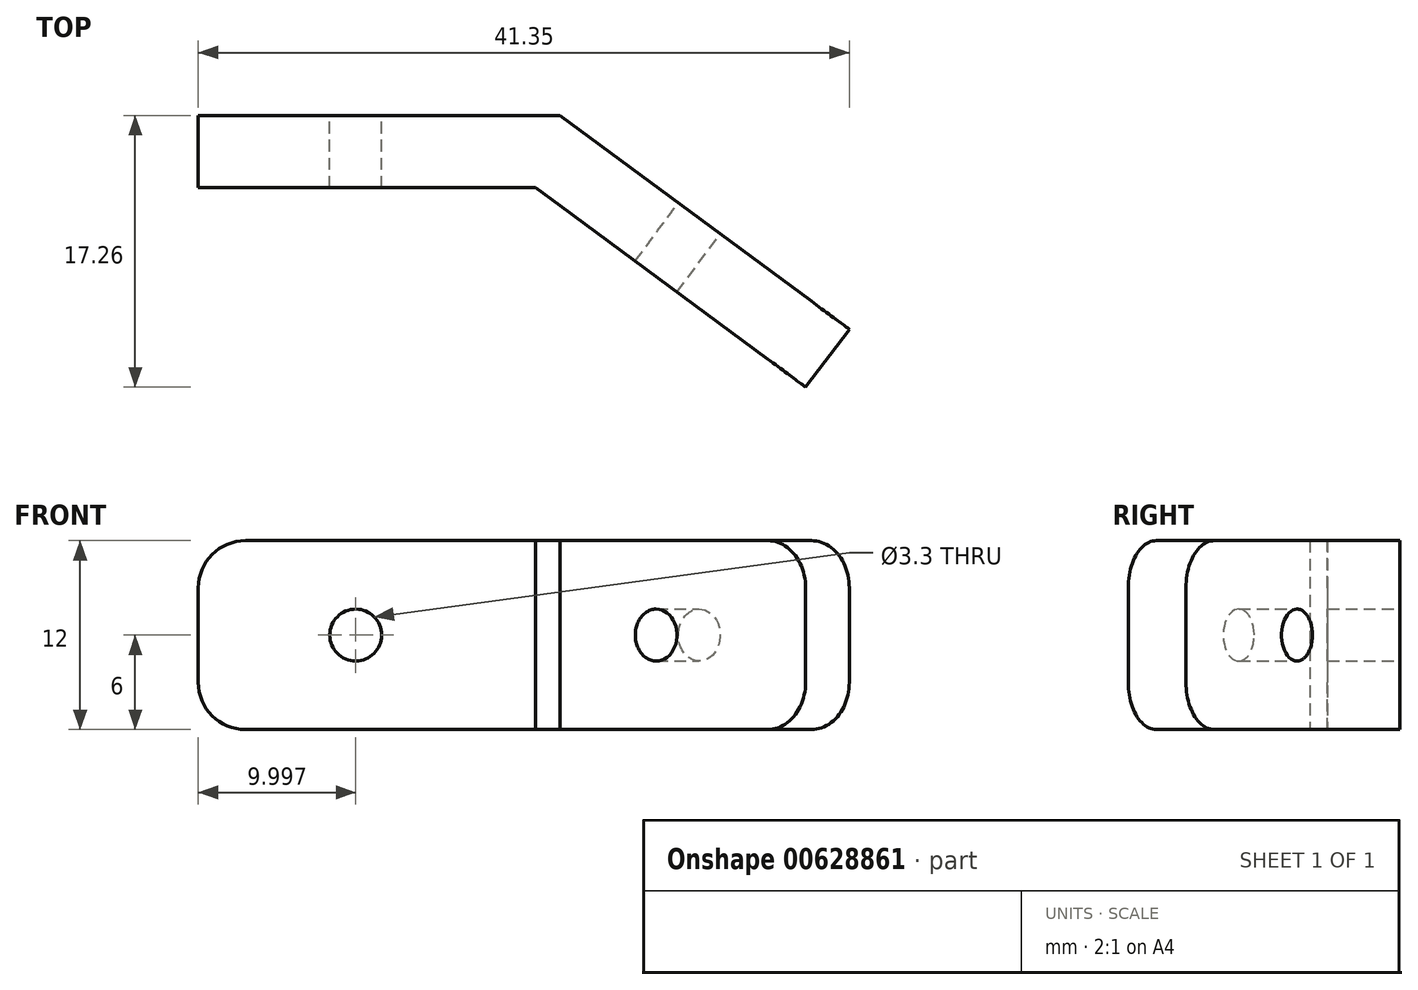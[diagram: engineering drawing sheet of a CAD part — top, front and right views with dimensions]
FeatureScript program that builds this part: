
annotation { "Feature Type Name" : "Feature", "Feature Type Description" : "" }
export const myFeature = defineFeature(function(context is Context, id is Id, definition is map)
    precondition{}
    {
        {
            var Q0;
            Q0=qCreatedBy(makeId("Top.planeOp"),FACE);
            var sketch = newSketch(context, id + "F0", { "sketchPlane" : qUnion([Q0])});
            skLineSegment(sketch, "E0", {"start": v(-22.97, 1.12) * mm, "end": v(-22.97, 5.72) * mm});
            skLineSegment(sketch, "E1", {"start": v(-22.97, 5.72) * mm, "end": v(0, 5.72) * mm});
            skLineSegment(sketch, "E2", {"start": v(-41.06, -47.79) * mm, "end": v(82.34, -47.79) * mm, "construction": true});
            skLineSegment(sketch, "E3", {"start": v(86.27, 5.72) * mm, "end": v(-90.07, 5.72) * mm, "construction": true});
            skLineSegment(sketch, "E4", {"start": v(0, 5.72) * mm, "end": v(72.37, -47.79) * mm, "construction": true});
            skLineSegment(sketch, "E5", {"start": v(0, 5.72) * mm, "end": v(18.38, -7.87) * mm});
            skLineSegment(sketch, "E6", {"start": v(0, 0) * mm, "end": v(15.6, -11.54) * mm});
            skLineSegment(sketch, "E7", {"start": v(15.6, -11.54) * mm, "end": v(18.38, -7.87) * mm});
            skLineSegment(sketch, "E8", {"start": v(0, 0) * mm, "end": v(2.73, 3.7) * mm});
            skLineSegment(sketch, "E9", {"start": v(-22.97, 1.12) * mm, "end": v(0.83, 1.12) * mm});
            skLineSegment(sketch, "E10", {"start": v(-1.57, 1.12) * mm, "end": v(0, 0) * mm});
            skSolve(sketch);
        }
        {
            var Q0;
            Q0=makeQuery(id+"F0.imprint","IMPRINT",FACE,{"disambiguationData":[TD([[makeQuery(id+"F0.imprint","IMPRINT",EDGE,{"derivedFrom":sQuery(id+"F0.wireOp",EDGE,"QjULmZR3-Fw54-M2tW-yVMf-iwzLRYVkHmLw")}),-1.0]])]});
            var Q1;
            {var subQ6=sQuery(id+"F0.wireOp",EDGE,"E0");Q1=makeQuery(id+"F0.imprint","IMPRINT",FACE,{"disambiguationData":[TD([[makeQuery(id+"F0.imprint","IMPRINT",EDGE,{"derivedFrom":subQ6}),-1.0]])]});}
            var Q2;
            {var subQ1=sQuery(id+"F0.wireOp",EDGE,"E6");Q2=makeQuery(id+"F0.imprint","IMPRINT",FACE,{"disambiguationData":[TD([[makeQuery(id+"F0.imprint","IMPRINT",EDGE,{"derivedFrom":subQ1}),1.0]])]});}
            var Q3;
            {var subQ0=sQuery(id+"F0.wireOp",EDGE,"E10");Q3=makeQuery(id+"F0.imprint","IMPRINT",FACE,{"disambiguationData":[TD([[makeQuery(id+"F0.imprint","IMPRINT",EDGE,{"derivedFrom":subQ0}),1.0]])]});}
            extrude(context, id + "F1", {"entities" : qUnion([Q0, Q1, Q2, Q3]), "depth" : 12 * mm});
        }
        {
            var Q0;
            Q0=makeQuery(id+"F1.opExtrude","SWEPT_FACE",FACE,{"disambiguationData":[OSD([sQuery(id+"F0.wireOp",EDGE,"E5")])]});
            var sketch = newSketch(context, id + "F2", { "sketchPlane" : qUnion([Q0])});
            skLineSegment(sketch, "E11", {"start": v(3.4, 6) * mm, "end": v(-19.46, 6) * mm, "construction": true});
            skCircle(sketch, "E12", {"center": v(-7.6, 6) * mm, "radius": 1.65 * mm});
            skSolve(sketch);
        }
        {
            var Q0;
            Q0=qSketchRegion(id+"F2",true);
            extrude(context, id + "F3", {"entities" : qUnion([Q0]), "operationType" : NewBodyOperationType.REMOVE, "endBound" : BoundingType.THROUGH_ALL, "oppositeDirection" : true, "depth" : 25 * mm});
        }
        {
            var Q0;
            Q0=makeQuery(id+"F1.opExtrude","SWEPT_FACE",FACE,{"disambiguationData":[OSD([sQuery(id+"F0.wireOp",EDGE,"E1")])]});
            var sketch = newSketch(context, id + "F4", { "sketchPlane" : qUnion([Q0])});
            skCircle(sketch, "E13", {"center": v(12.97, 6) * mm, "radius": 1.65 * mm});
            skLineSegment(sketch, "E14", {"start": v(0, 6) * mm, "end": v(22.97, 6) * mm, "construction": true});
            skSolve(sketch);
        }
        {
            var Q0;
            Q0=qSketchRegion(id+"F4",true);
            extrude(context, id + "F5", {"entities" : qUnion([Q0]), "operationType" : NewBodyOperationType.REMOVE, "endBound" : BoundingType.THROUGH_ALL, "oppositeDirection" : true, "depth" : 25 * mm});
        }
        {
            var Q0;
            Q0=makeQuery(id+"F1.opExtrude","CAP_EDGE",EDGE,{"disambiguationData":[OSD([sQuery(id+"F0.wireOp",EDGE,"E0")])],"isStart":false});
            var Q1;
            Q1=makeQuery(id+"F1.opExtrude","CAP_EDGE",EDGE,{"disambiguationData":[OSD([sQuery(id+"F0.wireOp",EDGE,"E0")])],"isStart":true});
            var Q2;
            Q2=makeQuery(id+"F1.opExtrude","CAP_EDGE",EDGE,{"disambiguationData":[OSD([sQuery(id+"F0.wireOp",EDGE,"E7")])],"isStart":true});
            var Q3;
            Q3=makeQuery(id+"F1.opExtrude","CAP_EDGE",EDGE,{"disambiguationData":[OSD([sQuery(id+"F0.wireOp",EDGE,"E7")])],"isStart":false});
            fillet(context, id + "F6", {"entities" : qUnion([Q0, Q1, Q2, Q3]), "radius" : 3 * mm, "tangentPropagation" : true, "allowEdgeOverflow" : false});
        }
    });
